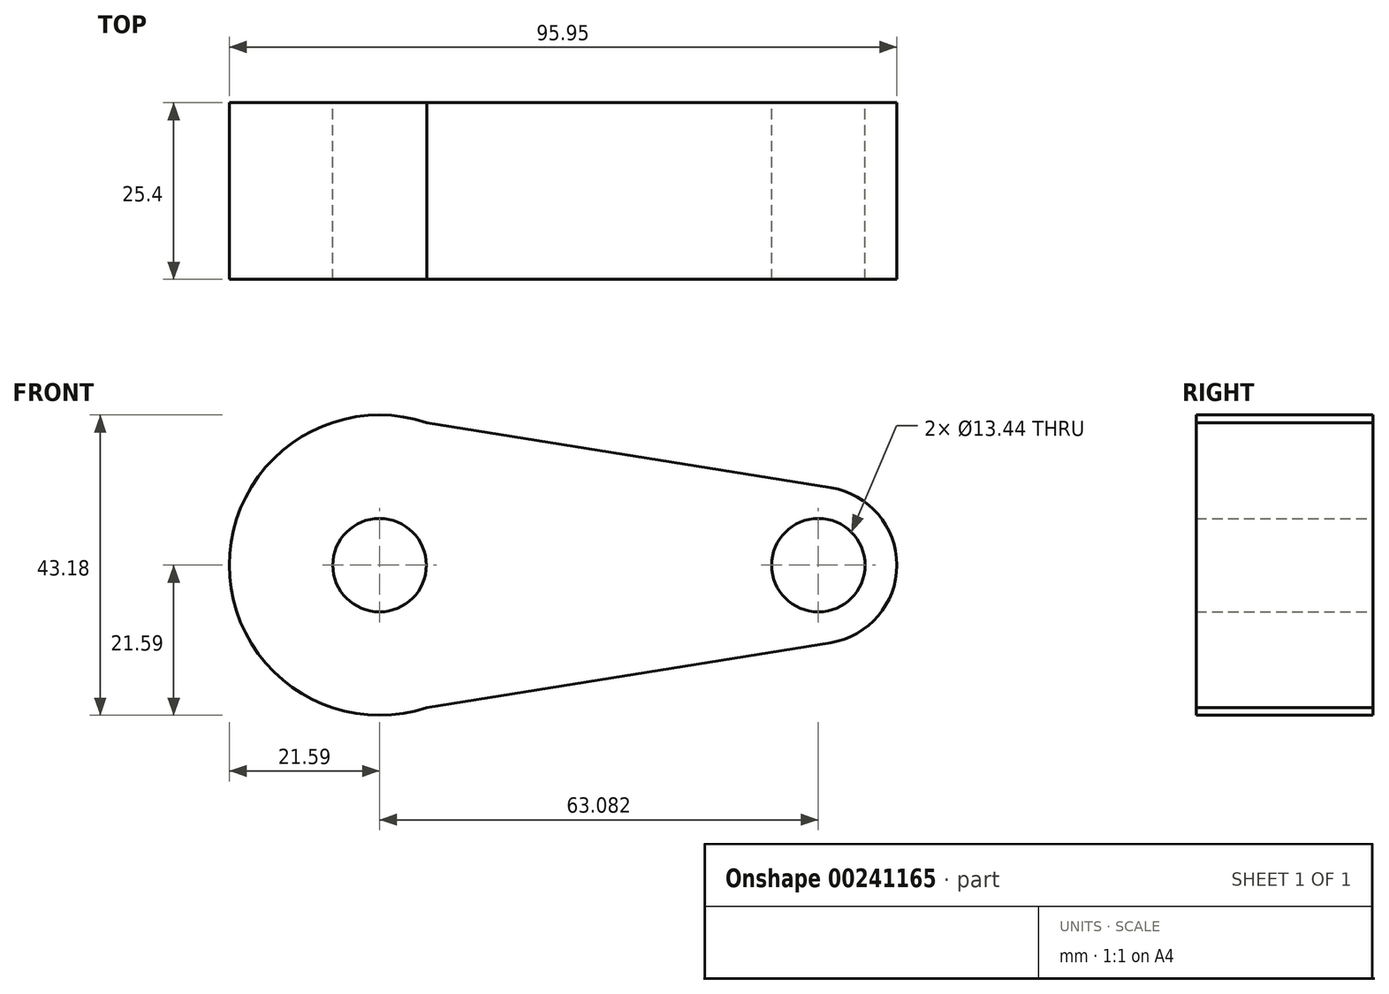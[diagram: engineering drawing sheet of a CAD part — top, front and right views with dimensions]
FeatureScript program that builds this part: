
annotation { "Feature Type Name" : "Feature", "Feature Type Description" : "" }
export const myFeature = defineFeature(function(context is Context, id is Id, definition is map)
    precondition{}
    {
        {
            var Q0;
            Q0=qCreatedBy(makeId("Front.planeOp"),FACE);
            var sketch = newSketch(context, id + "F0", { "sketchPlane" : qUnion([Q0])});
            skCircle(sketch, "E0", {"center": v(0, 0) * mm, "radius": 21.59 * mm});
            skCircle(sketch, "E1", {"center": v(63.08, 0) * mm, "radius": 11.28 * mm});
            skLineSegment(sketch, "E2", {"start": v(0, 21.59) * mm, "end": v(64.88, 11.13) * mm});
            skLineSegment(sketch, "E3", {"start": v(0, -21.59) * mm, "end": v(64.88, -11.13) * mm});
            skCircle(sketch, "E4", {"center": v(0, 0) * mm, "radius": 6.72 * mm});
            skCircle(sketch, "E5", {"center": v(63.08, 0) * mm, "radius": 6.72 * mm});
            skSolve(sketch);
        }
        {
            var Q0;
            Q0 = qSketchRegion(id + "F0", true);
            extrude(context, id + "F1", {"entities" : qUnion([Q0]), "depth" : 25.4 * mm});
        }
    });
